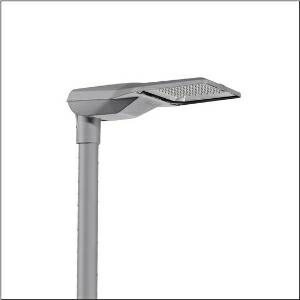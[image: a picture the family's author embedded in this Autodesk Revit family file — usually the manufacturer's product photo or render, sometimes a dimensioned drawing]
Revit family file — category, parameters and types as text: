
# Revit family: streetlight_sl_21_iq_midi___p0_5a_5xe3v31d08nb_4594
name_source: partatom
category: Lighting Fixtures
units: mm (PartAtom-declared; Revit-internal decimal feet)

## family parameters
Cut with Voids When Loaded = No
Host = Face
Light Source = No
Part Type = Normal
Room Calculation Point = No
Round Connector Dimension = Use Diameter
Shared = No

## types (1)
- --- (1 x LED, 22830 lm, 155.5 W, 3000K)
    Apparent Load = 155 VA
    CIE Flux Codes = 37 73 96 100 100
    Color Rendering = 70
    Color Temperature = 3000K
    Default Elevation = 1800 mm
    Description = Streetlight SL 21 iQ midi, mast luminaire, primary light control with lens, of PMMA, primary optical cover: cover, of toughened safety glass, transparent, light distribution: P0.5a, light emission: direct distribution, primary light characteristic: asymmetric, installation type: post-top, side-entry, LED, High Power LED, rated luminous flux: 22.830lm, luminous efficacy: 147lm/W, light colour: 730, colour temperature: 3000K, control gear: iQ-Comfort, control: pre-setting: linear dimming characteristic, Auto-Match, Temp-Guard, Lumen-Switch, Night-Set, Smart-Wire, Light-Fading, Desk-Remote (wireless, voltage-free reading and setting of iQ features in the workshop via application-optimized NFC function/RFID function), optimised constant luminous flux control (CLO 2.0), mains connection: 230..240V, AC, 50/60Hz, start of lifetime: 156W, end of service life: 162W, reduction: 69W, luminaire housing, of diecast aluminium, powder-coated, Siteco® metallic grey (DB 702S), corrosivity category C5 mid according to DIN EN ISO 12944, please order mast flange separately, inclination adjustable: 0°, 5°, 10°, 15°, sealing non-destructively replaceable, multi-level sealing system, length: 644mm, width: 335mm, height: 110mm, mast flange for spigot size: 42mm (side-entry): 5XC10008XM4, 60/48mm (side-entry/post-top): 5XC10108XM2, 76/60mm (side-entry/post-top): 5XC10108XM1, mounting height: 4..8m, protection rating (complete): IP66, insulation class (complete): insulation class II (safety insulation), certification: CE, ENEC, ENEC+, VDE, impact resistance: IK09, permissible operating ambient temperature for outdoor applications: -40..+50°C, standard-compliant lighting for roads and squares, packaging unit: 1 piece

Light Distribution: P0.5a
    Height = 111 mm
    Lamp = 1 x LED
    Lamp Light Flux = 22830 lm
    Lamp Power = 155.5 W
    Lamp count = 1
    Length = 644 mm
    Luminous efficacy = 147 lm/W
    Manufacturer = Siteco
    ModVariant = No
    Model = 5XE3V31D08NB
    Number of Poles = 1
    OnlyDefault = Yes
    Power Factor = 1
    Product Name = Streetlight SL 21 iQ midi | P0.5a
    Product group = mast luminaire | pylon top
    ProductGroupID = 6100
    Protection Class = Protection class II
    Protection Degree = IP 66
    RLX_Detail_Level = 1
    RLX_Emergency_Light_Flux = 0 lm
    RLX_Emergency_Type = 0
    RLX_Emergency_Type_DB = No
    RlxData = <blob elided: 91193 chars, md5=ad1fa282>
    Socket = socket
    Standby Power = 0 W
    System Light Flux = 22831 lm
    System Power = 155 W
    Type Comments = factory setting: luminous flux: 100 % | dim-lin: 254 | 823 mA
    Type Image = l_1004298.jpg
    URL = http://relux.com
    VarID = @adj_066088
    Voltage = 0 V
    Weight = 0.00 kg
    Width = 336 mm

## geometry (parser evidence)
native form markers: Blend x4, Sweep x11
no freeform markers — native parametric forms only
